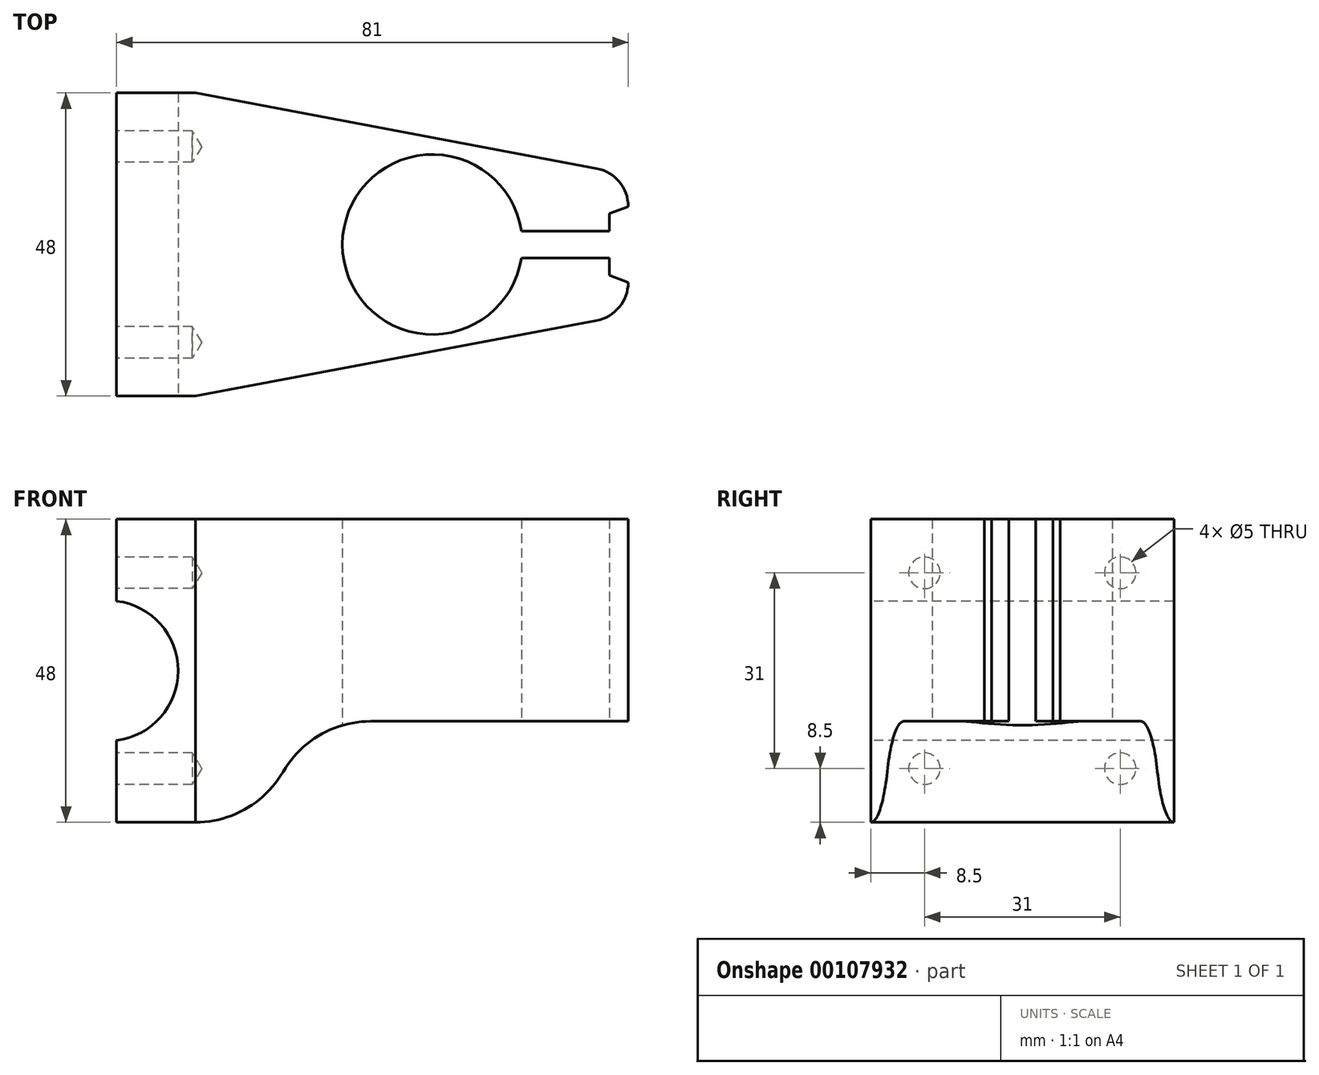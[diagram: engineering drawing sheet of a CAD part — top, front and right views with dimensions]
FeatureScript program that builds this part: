
annotation { "Feature Type Name" : "Feature", "Feature Type Description" : "" }
export const myFeature = defineFeature(function(context is Context, id is Id, definition is map)
    precondition{}
    {
        {
            var Q0;
            Q0=qCreatedBy(makeId("Top.planeOp"),FACE);
            var sketch = newSketch(context, id + "F0", { "sketchPlane" : qUnion([Q0])});
            skLineSegment(sketch, "E0", {"start": v(-37.13, 0) * mm, "end": v(43.87, 0) * mm, "construction": true});
            skLineSegment(sketch, "E1", {"start": v(-37.13, 24) * mm, "end": v(-24.63, 24) * mm});
            skLineSegment(sketch, "E2", {"start": v(-24.63, 24) * mm, "end": v(38.87, 12.03) * mm});
            skLineSegment(sketch, "E3", {"start": v(-37.13, 0) * mm, "end": v(-37.13, 24) * mm});
            skLineSegment(sketch, "E4", {"start": v(26.96, 2.13) * mm, "end": v(40.87, 2.13) * mm});
            skLineSegment(sketch, "E5", {"start": v(40.87, 2.13) * mm, "end": v(40.87, 4.87) * mm});
            skLineSegment(sketch, "E6", {"start": v(40.87, 4.87) * mm, "end": v(43.87, 6) * mm});
            skArc(sketch, "E7", {"start": v(43.87, 6) * mm, "mid": v(42.46, 9.92) * mm, "end": v(38.87, 12.03) * mm});
            skLineSegment(sketch, "E8.MirrorCS", {"start": v(26.96, -2.12) * mm, "end": v(40.87, -2.12) * mm});
            skLineSegment(sketch, "E9.MirrorCS", {"start": v(40.87, -2.13) * mm, "end": v(40.87, -4.88) * mm});
            skLineSegment(sketch, "E10.MirrorCS", {"start": v(40.87, -4.88) * mm, "end": v(43.87, -6) * mm});
            skArc(sketch, "E11.MirrorCS", {"start": v(43.87, -6) * mm, "mid": v(42.46, -9.92) * mm, "end": v(38.87, -12.03) * mm});
            skLineSegment(sketch, "E12.MirrorCS", {"start": v(-24.63, -24) * mm, "end": v(38.87, -12.03) * mm});
            skLineSegment(sketch, "E13.MirrorCS", {"start": v(-37.13, 0) * mm, "end": v(-37.13, -24) * mm});
            skLineSegment(sketch, "E14.MirrorCS", {"start": v(-37.13, -24) * mm, "end": v(-24.63, -24) * mm});
            skArc(sketch, "E15", {"start": v(26.96, 2.13) * mm, "mid": v(-1.38, 0) * mm, "end": v(26.96, -2.13) * mm});
            skLineSegment(sketch, "E16", {"start": v(43.87, 6) * mm, "end": v(43.87, 0) * mm, "construction": true});
            skSolve(sketch);
        }
        {
            var Q0;
            Q0 = qSketchRegion(id + "F0", true);
            extrude(context, id + "F1", {"entities" : qUnion([Q0]), "endBound" : BoundingType.SYMMETRIC, "depth" : 48 * mm});
        }
        {
            var Q0;
            Q0=makeQuery(id+"F1.opExtrude","SWEPT_FACE",FACE,{"disambiguationData":[OSD([sQuery(id+"F0.wireOp",EDGE,"E14.MirrorCS")])]});
            var sketch = newSketch(context, id + "F2", { "sketchPlane" : qUnion([Q0])});
            skArc(sketch, "E17", {"start": v(-24.63, -24) * mm, "mid": v(-16.63, -21.86) * mm, "end": v(-10.77, -16) * mm});
            skArc(sketch, "E18", {"start": v(3.08, -8) * mm, "mid": v(-4.92, -10.14) * mm, "end": v(-10.77, -16) * mm});
            skLineSegment(sketch, "E19", {"start": v(3.08, -8) * mm, "end": v(48.1, -8) * mm});
            skLineSegment(sketch, "E20", {"start": v(-24.63, -24) * mm, "end": v(48.1, -24) * mm});
            skLineSegment(sketch, "E21", {"start": v(48.1, -24) * mm, "end": v(48.1, -8) * mm});
            skSolve(sketch);
        }
        {
            var Q0;
            Q0 = qSketchRegion(id + "F2", true);
            var Q1;
            Q1=makeQuery(id+"F1.opExtrude","SWEPT_FACE",FACE,{"disambiguationData":[OSD([sQuery(id+"F0.wireOp",EDGE,"E1")])]});
            extrude(context, id + "F3", {"entities" : qUnion([Q0]), "operationType" : NewBodyOperationType.REMOVE, "endBound" : BoundingType.UP_TO_SURFACE, "oppositeDirection" : true, "endBoundEntityFace" : qUnion([Q1]), "depth" : 25 * mm});
        }
        {
            var Q0;
            Q0=makeQuery(id+"F1.opExtrude","SWEPT_FACE",FACE,{"disambiguationData":[OSD([sQuery(id+"F0.wireOp",EDGE,"E14.MirrorCS")])]});
            var sketch = newSketch(context, id + "F4", { "sketchPlane" : qUnion([Q0])});
            skArc(sketch, "E22", {"start": v(-37.13, -11.03) * mm, "mid": v(-27.38, 0) * mm, "end": v(-37.13, 11.03) * mm});
            skLineSegment(sketch, "E23", {"start": v(5.72, 0) * mm, "end": v(-37.13, 0) * mm, "construction": true});
            skLineSegment(sketch, "E24", {"start": v(-37.13, 11.03) * mm, "end": v(-37.13, -11.03) * mm});
            skSolve(sketch);
        }
        {
            var Q0;
            Q0 = qSketchRegion(id + "F4", true);
            var Q1;
            Q1=makeQuery(id+"F1.opExtrude","SWEPT_FACE",FACE,{"disambiguationData":[OSD([sQuery(id+"F0.wireOp",EDGE,"E1")])]});
            extrude(context, id + "F5", {"entities" : qUnion([Q0]), "operationType" : NewBodyOperationType.REMOVE, "endBound" : BoundingType.UP_TO_SURFACE, "oppositeDirection" : true, "endBoundEntityFace" : qUnion([Q1]), "depth" : 25 * mm});
        }
        {
            var Q0;
            {var subQ0=sQuery(id+"F0.wireOp",EDGE,"E1");var subQ1=sQuery(id+"F0.wireOp",EDGE,"E14.MirrorCS");var subQ2=sQuery(id+"F0.wireOp",EDGE,"E13.MirrorCS");var subQ3=sQuery(id+"F0.wireOp",EDGE,"E3");Q0=makeQuery(id+"F5.boolean.opBoolean","SPLIT",FACE,{"disambiguationData":[TD([makeQuery(id+"F1.opExtrude","CAP_FACE",FACE,{"disambiguationData":[OSD([subQ0,sQuery(id+"F0.wireOp",EDGE,"E2"),subQ3,sQuery(id+"F0.wireOp",EDGE,"E4"),sQuery(id+"F0.wireOp",EDGE,"E5"),sQuery(id+"F0.wireOp",EDGE,"E6"),sQuery(id+"F0.wireOp",EDGE,"E7"),sQuery(id+"F0.wireOp",EDGE,"E8.MirrorCS"),sQuery(id+"F0.wireOp",EDGE,"E9.MirrorCS"),sQuery(id+"F0.wireOp",EDGE,"E10.MirrorCS"),sQuery(id+"F0.wireOp",EDGE,"E11.MirrorCS"),sQuery(id+"F0.wireOp",EDGE,"E12.MirrorCS"),subQ2,subQ1,sQuery(id+"F0.wireOp",EDGE,"E15")])],"isStart":false})])],"derivedFrom":makeQuery(id+"F1.opExtrude","SWEPT_FACE",FACE,{"disambiguationData":[OSD([subQ3,subQ2])]})});}
            var sketch = newSketch(context, id + "F6", { "sketchPlane" : qUnion([Q0])});
            skPoint(sketch, "E25", {"position": v(-15.5, 15.5) * mm});
            skPoint(sketch, "E26.1.0", {"position": v(15.5, 15.5) * mm});
            skPoint(sketch, "E26.2.0", {"position": v(15.5, -15.5) * mm});
            skPoint(sketch, "E26.3.0", {"position": v(-15.5, -15.5) * mm});
            skPoint(sketch, "E26.center", {"position": v(0, 0) * mm});
            skLineSegment(sketch, "E26.anchor1", {"start": v(0, 0) * mm, "end": v(-15.5, 15.5) * mm, "construction": true});
            skLineSegment(sketch, "E26.anchor2", {"start": v(0, 0) * mm, "end": v(-15.5, -15.5) * mm, "construction": true});
            skSolve(sketch);
        }
        {
            var Q0;
            Q0=sQuery(id+"F6.wireOp",VERTEX,"E25");
            var Q1;
            Q1=sQuery(id+"F6.wireOp",VERTEX,"E26.1.0");
            var Q2;
            Q2=sQuery(id+"F6.wireOp",VERTEX,"E26.2.0");
            var Q3;
            Q3=sQuery(id+"F6.wireOp",VERTEX,"E26.3.0");
            var Q4;
            Q4=makeQuery(id+"F1.opExtrude","SWEPT_BODY",BODY,{"disambiguationData":[OSD([sQuery(id+"F0.wireOp",EDGE,"E1"),sQuery(id+"F0.wireOp",EDGE,"E2"),sQuery(id+"F0.wireOp",EDGE,"E3"),sQuery(id+"F0.wireOp",EDGE,"E4"),sQuery(id+"F0.wireOp",EDGE,"E5"),sQuery(id+"F0.wireOp",EDGE,"E6"),sQuery(id+"F0.wireOp",EDGE,"E7"),sQuery(id+"F0.wireOp",EDGE,"E8.MirrorCS"),sQuery(id+"F0.wireOp",EDGE,"E9.MirrorCS"),sQuery(id+"F0.wireOp",EDGE,"E10.MirrorCS"),sQuery(id+"F0.wireOp",EDGE,"E11.MirrorCS"),sQuery(id+"F0.wireOp",EDGE,"E12.MirrorCS"),sQuery(id+"F0.wireOp",EDGE,"E13.MirrorCS"),sQuery(id+"F0.wireOp",EDGE,"E14.MirrorCS"),sQuery(id+"F0.wireOp",EDGE,"E15")])]});
            hole(context, id + "F7", {"style" : HoleStyle.SIMPLE, "endStyle" : HoleEndStyle.BLIND, "holeDiameter" : 5 * mm, "holeDepth" : 12 * mm, "startFromSketch" : true, "locations" : qUnion([Q0, Q1, Q2, Q3]), "scope" : qUnion([Q4])});
        }
    });
